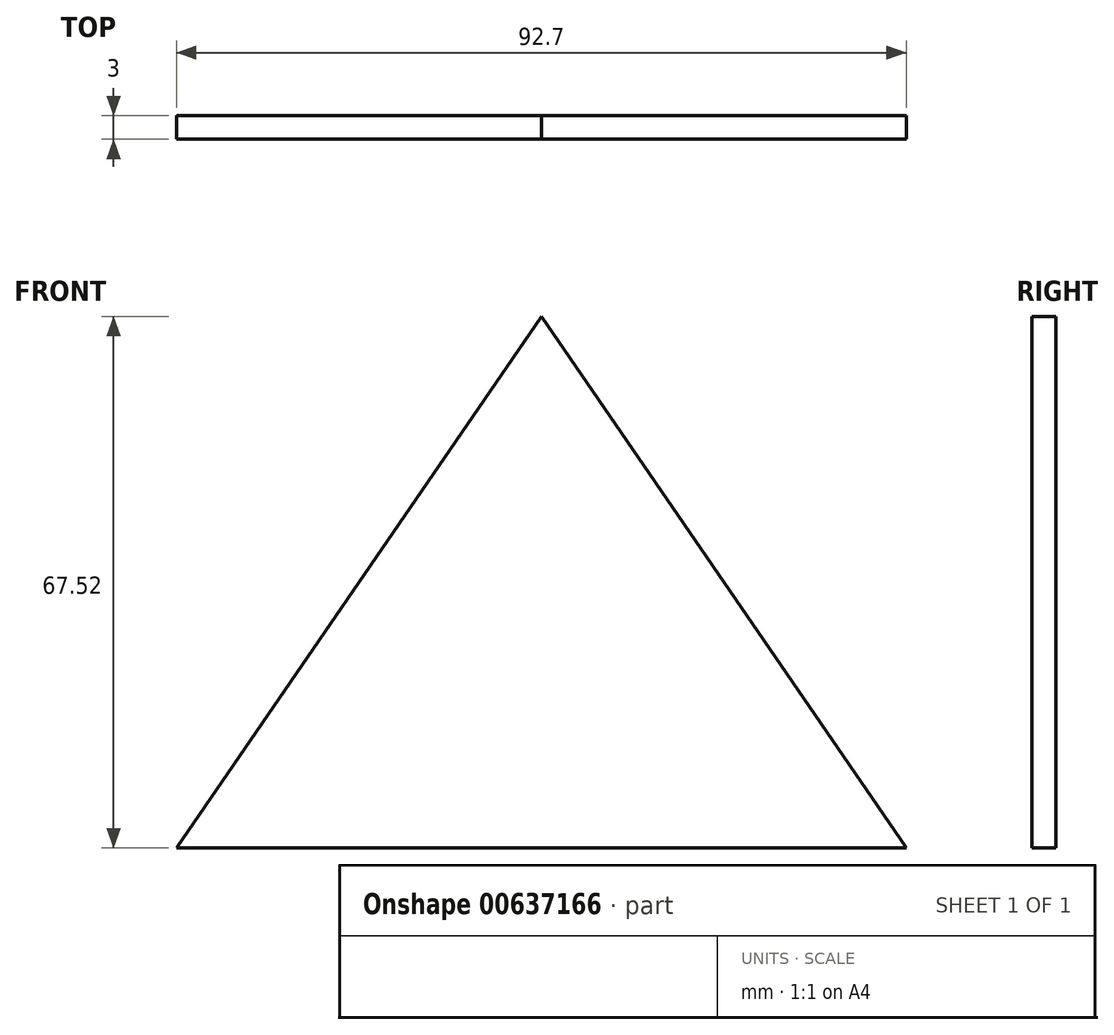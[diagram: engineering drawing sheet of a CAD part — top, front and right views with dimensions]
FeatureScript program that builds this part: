
annotation { "Feature Type Name" : "Feature", "Feature Type Description" : "" }
export const myFeature = defineFeature(function(context is Context, id is Id, definition is map)
    precondition{}
    {
        {
            var Q0;
            Q0=qCreatedBy(makeId("Front.planeOp"),FACE);
            var sketch = newSketch(context, id + "F0", { "sketchPlane" : qUnion([Q0])});
            skLineSegment(sketch, "E0", {"start": v(0, 0) * mm, "end": v(46.35, 0) * mm});
            skLineSegment(sketch, "E1", {"start": v(0, 0) * mm, "end": v(0, 67.52) * mm, "construction": true});
            skLineSegment(sketch, "E2", {"start": v(0, 67.52) * mm, "end": v(46.35, 0) * mm});
            skLineSegment(sketch, "E3.MirrorCS", {"start": v(0, 67.52) * mm, "end": v(-46.35, 0) * mm});
            skLineSegment(sketch, "E4.MirrorCS", {"start": v(0, 0) * mm, "end": v(-46.35, 0) * mm});
            skSolve(sketch);
        }
        {
            var Q0;
            Q0=makeQuery(id+"F0.imprint","IMPRINT",FACE,{"disambiguationData":[TD([[makeQuery(id+"F0.imprint","IMPRINT",EDGE,{"derivedFrom":sQuery(id+"F0.wireOp",EDGE,"E0")}),1.0]])]});
            extrude(context, id + "F1", {"entities" : qUnion([Q0]), "depth" : 3 * mm, "offsetDistance" : 25 * mm});
        }
    });
